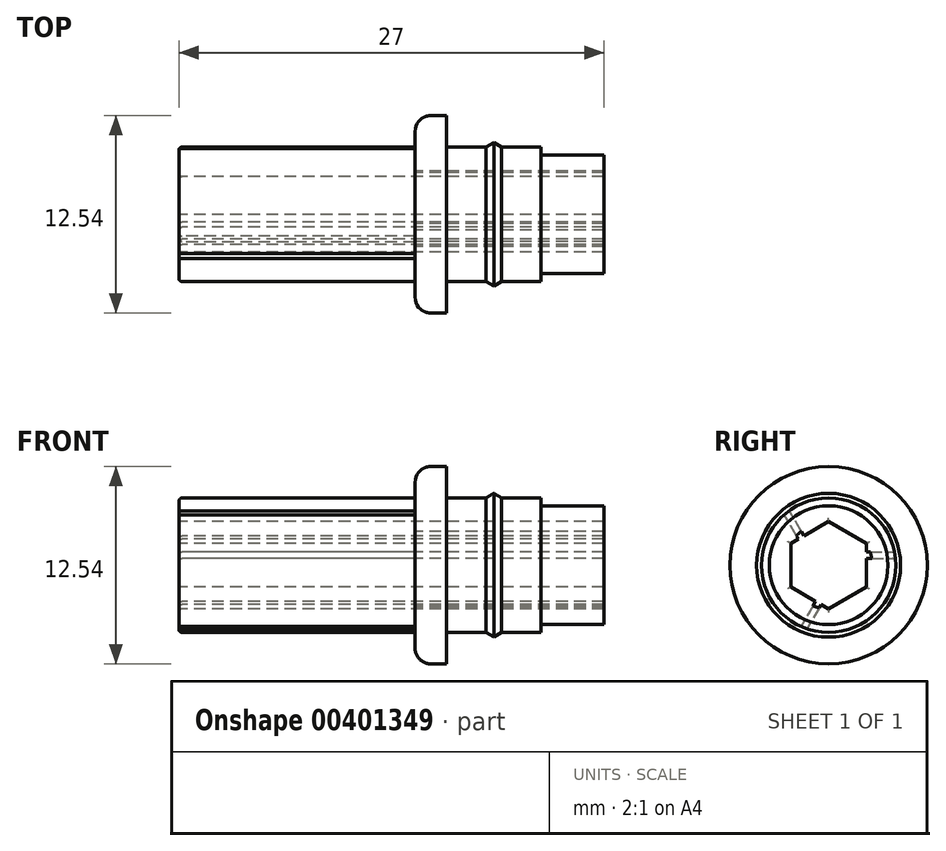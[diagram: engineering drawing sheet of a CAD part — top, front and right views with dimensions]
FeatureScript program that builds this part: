
annotation { "Feature Type Name" : "Feature", "Feature Type Description" : "" }
export const myFeature = defineFeature(function(context is Context, id is Id, definition is map)
    precondition{}
    {
        {
            var Q0;
            Q0=qCreatedBy(makeId("Front.planeOp"),FACE);
            var sketch = newSketch(context, id + "F0", { "sketchPlane" : qUnion([Q0])});
            skLineSegment(sketch, "E0", {"start": v(-9.05, 2.77) * mm, "end": v(17.95, 2.77) * mm});
            skLineSegment(sketch, "E1", {"start": v(7.95, 4.27) * mm, "end": v(7.95, 6.27) * mm});
            skLineSegment(sketch, "E2", {"start": v(7.95, 6.27) * mm, "end": v(5.95, 6.27) * mm});
            skLineSegment(sketch, "E3", {"start": v(5.95, 6.27) * mm, "end": v(5.95, 4.27) * mm});
            skLineSegment(sketch, "E4", {"start": v(5.95, 4.27) * mm, "end": v(-9.05, 4.27) * mm});
            skLineSegment(sketch, "E5", {"start": v(-9.05, 4.27) * mm, "end": v(-9.05, 2.77) * mm});
            skLineSegment(sketch, "E6", {"start": v(-9.05, 0) * mm, "end": v(13.38, 0) * mm});
            skLineSegment(sketch, "E7", {"start": v(10.45, 4.27) * mm, "end": v(7.95, 4.27) * mm});
            skLineSegment(sketch, "E8", {"start": v(10.45, 4.27) * mm, "end": v(10.95, 4.57) * mm});
            skLineSegment(sketch, "E9", {"start": v(10.95, 4.57) * mm, "end": v(11.45, 4.27) * mm});
            skLineSegment(sketch, "E10", {"start": v(11.45, 4.27) * mm, "end": v(13.95, 4.27) * mm});
            skLineSegment(sketch, "E11", {"start": v(13.95, 4.27) * mm, "end": v(13.95, 3.77) * mm});
            skLineSegment(sketch, "E12", {"start": v(13.95, 3.77) * mm, "end": v(17.95, 3.77) * mm});
            skLineSegment(sketch, "E13", {"start": v(17.95, 3.77) * mm, "end": v(17.95, 2.77) * mm});
            skSolve(sketch);
        }
        {
            var Q0;
            Q0=makeQuery(id+"F0.imprint","IMPRINT",FACE,{"disambiguationData":[TD([[makeQuery(id+"F0.imprint","IMPRINT",EDGE,{"derivedFrom":sQuery(id+"F0.wireOp",EDGE,"E0")}),1.0]])]});
            var Q1;
            Q1=sQuery(id+"F0.wireOp",EDGE,"E6");
            revolve(context, id + "F1", {"entities" : qUnion([Q0]), "axis" : qUnion([Q1]), "revolveType" : RevolveType.FULL});
        }
        {
            var Q0;
            Q0=makeQuery(id+"F1.opRevolve","SWEPT_EDGE",EDGE,{"disambiguationData":[OSD([sQuery(id+"F0.wireOp",EDGE,"E2"),sQuery(id+"F0.wireOp",EDGE,"E3")])]});
            fillet(context, id + "F2", {"entities" : qUnion([Q0]), "radius" : 1 * mm, "tangentPropagation" : true, "allowEdgeOverflow" : false});
        }
        {
            var Q0;
            Q0=makeQuery(id+"F1.opRevolve","SWEPT_FACE",FACE,{"disambiguationData":[OSD([sQuery(id+"F0.wireOp",EDGE,"E5")])]});
            var sketch = newSketch(context, id + "F3", { "sketchPlane" : qUnion([Q0])});
            skCircle(sketch, "E14.cCircle", {"center": v(0, 0) * mm, "radius": 2.4 * mm, "construction": true});
            skLineSegment(sketch, "E14.0", {"start": v(2.4, 1.38) * mm, "end": v(2.4, -1.38) * mm});
            skLineSegment(sketch, "E14.1", {"start": v(2.4, -1.38) * mm, "end": v(0, -2.77) * mm});
            skLineSegment(sketch, "E14.2", {"start": v(0, -2.77) * mm, "end": v(-2.4, -1.38) * mm});
            skLineSegment(sketch, "E14.3", {"start": v(-2.4, -1.38) * mm, "end": v(-2.4, 1.38) * mm});
            skLineSegment(sketch, "E14.4", {"start": v(-2.4, 1.38) * mm, "end": v(0, 2.77) * mm});
            skLineSegment(sketch, "E14.5", {"start": v(0, 2.77) * mm, "end": v(2.4, 1.38) * mm});
            skPoint(sketch, "E14.0.midPoint", {"position": v(2.4, 0) * mm});
            skLineSegment(sketch, "E15", {"start": v(1.58, 1.86) * mm, "end": v(2.5, 3.46) * mm});
            skLineSegment(sketch, "E16", {"start": v(1.92, 1.66) * mm, "end": v(2.82, 3.2) * mm});
            skLineSegment(sketch, "E17", {"start": v(0.82, -2.3) * mm, "end": v(1.75, -3.9) * mm});
            skLineSegment(sketch, "E18", {"start": v(0.48, -2.5) * mm, "end": v(1.37, -4.04) * mm});
            skLineSegment(sketch, "E19", {"start": v(-2.4, 0.83) * mm, "end": v(-4.19, 0.83) * mm});
            skLineSegment(sketch, "E20", {"start": v(-2.4, 0.43) * mm, "end": v(-4.25, 0.43) * mm});
            skSolve(sketch);
        }
        {
            var Q0;
            {var subQ0=sQuery(id+"F3.wireOp",EDGE,"E14.0");Q0=makeQuery(id+"F3.imprint","IMPRINT",FACE,{"disambiguationData":[TD([[makeQuery(id+"F3.imprint","IMPRINT",EDGE,{"derivedFrom":subQ0}),1.0]])]});}
            extrude(context, id + "F4", {"entities" : qUnion([Q0]), "operationType" : NewBodyOperationType.ADD, "depth" : -27 * mm});
        }
        {
            var Q0;
            {var subQ0=sQuery(id+"F3.wireOp",EDGE,"E14.1");Q0=makeQuery(id+"F3.imprint","IMPRINT",FACE,{"disambiguationData":[TD([[makeQuery(id+"F3.imprint","IMPRINT",EDGE,{"derivedFrom":subQ0}),1.0]])]});}
            var Q1;
            {var subQ0=sQuery(id+"F3.wireOp",EDGE,"E14.2");Q1=makeQuery(id+"F3.imprint","IMPRINT",FACE,{"disambiguationData":[TD([[makeQuery(id+"F3.imprint","IMPRINT",EDGE,{"derivedFrom":subQ0}),1.0]])]});}
            var Q2;
            {var subQ0=sQuery(id+"F3.wireOp",EDGE,"E14.3");Q2=makeQuery(id+"F3.imprint","IMPRINT",FACE,{"disambiguationData":[TD([[makeQuery(id+"F3.imprint","IMPRINT",EDGE,{"derivedFrom":subQ0}),1.0]])]});}
            var Q3;
            {var subQ0=sQuery(id+"F3.wireOp",EDGE,"E14.4");Q3=makeQuery(id+"F3.imprint","IMPRINT",FACE,{"disambiguationData":[TD([[makeQuery(id+"F3.imprint","IMPRINT",EDGE,{"derivedFrom":subQ0}),1.0]])]});}
            var Q4;
            {var subQ0=sQuery(id+"F3.wireOp",EDGE,"E14.5");Q4=makeQuery(id+"F3.imprint","IMPRINT",FACE,{"disambiguationData":[TD([[makeQuery(id+"F3.imprint","IMPRINT",EDGE,{"derivedFrom":subQ0}),1.0]])]});}
            var Q5;
            {var subQ0=sQuery(id+"F3.wireOp",EDGE,"E14.0");Q5=makeQuery(id+"F3.imprint","IMPRINT",FACE,{"disambiguationData":[TD([[makeQuery(id+"F3.imprint","IMPRINT",EDGE,{"derivedFrom":subQ0}),1.0]])]});}
            extrude(context, id + "F5", {"entities" : qUnion([Q0, Q1, Q2, Q3, Q4, Q5]), "operationType" : NewBodyOperationType.ADD, "depth" : -27 * mm});
        }
        {
            var Q0;
            {var subQ0=sQuery(id+"F3.wireOp",EDGE,"E15");var subQ1=sQuery(id+"F0.wireOp",EDGE,"E5");var subQ2=makeQuery(id+"F1.opRevolve","SWEPT_EDGE",EDGE,{"disambiguationData":[OSD([sQuery(id+"F0.wireOp",EDGE,"E4"),subQ1])]});var subQ3=makeQuery(id+"F3.imprint","INTERSECT",VERTEX,{"derivedFrom":[subQ2,subQ0]});Q0=makeQuery(id+"F3.imprint","IMPRINT",FACE,{"disambiguationData":[TD([[makeQuery(id+"F3.imprint","IMPRINT",EDGE,{"disambiguationData":[TD([[subQ3,1.0]])],"derivedFrom":subQ0}),-1.0]])]});}
            extrude(context, id + "F6", {"entities" : qUnion([Q0]), "operationType" : NewBodyOperationType.REMOVE, "oppositeDirection" : true, "depth" : 15 * mm});
        }
        {
            var Q0;
            {var subQ0=sQuery(id+"F3.wireOp",EDGE,"E17");var subQ1=sQuery(id+"F0.wireOp",EDGE,"E5");var subQ2=makeQuery(id+"F1.opRevolve","SWEPT_EDGE",EDGE,{"disambiguationData":[OSD([sQuery(id+"F0.wireOp",EDGE,"E4"),subQ1])]});var subQ3=makeQuery(id+"F3.imprint","INTERSECT",VERTEX,{"derivedFrom":[subQ2,subQ0]});Q0=makeQuery(id+"F3.imprint","IMPRINT",FACE,{"disambiguationData":[TD([[makeQuery(id+"F3.imprint","IMPRINT",EDGE,{"disambiguationData":[TD([[subQ3,1.0]])],"derivedFrom":subQ0}),-1.0]])]});}
            extrude(context, id + "F7", {"entities" : qUnion([Q0]), "operationType" : NewBodyOperationType.REMOVE, "oppositeDirection" : true, "depth" : 15 * mm});
        }
        {
            var Q0;
            {var subQ0=sQuery(id+"F3.wireOp",EDGE,"E19");var subQ1=sQuery(id+"F0.wireOp",EDGE,"E5");var subQ2=makeQuery(id+"F1.opRevolve","SWEPT_EDGE",EDGE,{"disambiguationData":[OSD([sQuery(id+"F0.wireOp",EDGE,"E4"),subQ1])]});var subQ3=makeQuery(id+"F3.imprint","INTERSECT",VERTEX,{"derivedFrom":[subQ2,subQ0]});Q0=makeQuery(id+"F3.imprint","IMPRINT",FACE,{"disambiguationData":[TD([[makeQuery(id+"F3.imprint","IMPRINT",EDGE,{"disambiguationData":[TD([[subQ3,1.0]])],"derivedFrom":subQ0}),1.0]])]});}
            extrude(context, id + "F8", {"entities" : qUnion([Q0]), "operationType" : NewBodyOperationType.REMOVE, "oppositeDirection" : true, "depth" : 15 * mm});
        }
        {
            var Q0;
            {var subQ0=sQuery(id+"F3.wireOp",EDGE,"E15");var subQ2=sQuery(id+"F0.wireOp",EDGE,"E5");var subQ6=sQuery(id+"F0.wireOp",EDGE,"E4");var subQ19=makeQuery(id+"F5.opExtrude","SWEPT_FACE",FACE,{"disambiguationData":[OSD([subQ0])]});Q0=makeQuery(id+"F8.boolean.opBoolean","SPLIT",EDGE,{"disambiguationData":[TD([subQ19])],"derivedFrom":makeQuery(id+"F7.boolean.opBoolean","SPLIT",EDGE,{"disambiguationData":[TD([subQ19])],"derivedFrom":makeQuery(id+"F1.opRevolve","SWEPT_EDGE",EDGE,{"disambiguationData":[OSD([subQ6,subQ2])]})})});}
            var Q1;
            {var subQ1=sQuery(id+"F0.wireOp",EDGE,"E5");var subQ3=sQuery(id+"F0.wireOp",EDGE,"E4");var subQ7=sQuery(id+"F3.wireOp",EDGE,"E16");Q1=makeQuery(id+"F7.boolean.opBoolean","SPLIT",EDGE,{"disambiguationData":[TD([makeQuery(id+"F5.opExtrude","SWEPT_FACE",FACE,{"disambiguationData":[OSD([subQ7])]})])],"derivedFrom":makeQuery(id+"F1.opRevolve","SWEPT_EDGE",EDGE,{"disambiguationData":[OSD([subQ3,subQ1])]})});}
            var Q2;
            {var subQ0=sQuery(id+"F3.wireOp",EDGE,"E15");var subQ2=sQuery(id+"F0.wireOp",EDGE,"E5");var subQ6=sQuery(id+"F0.wireOp",EDGE,"E4");var subQ10=sQuery(id+"F3.wireOp",EDGE,"E18");var subQ15=makeQuery(id+"F5.opExtrude","SWEPT_FACE",FACE,{"disambiguationData":[OSD([subQ10])]});Q2=makeQuery(id+"F8.boolean.opBoolean","SPLIT",EDGE,{"disambiguationData":[TD([subQ15])],"derivedFrom":makeQuery(id+"F7.boolean.opBoolean","SPLIT",EDGE,{"disambiguationData":[TD([makeQuery(id+"F5.opExtrude","SWEPT_FACE",FACE,{"disambiguationData":[OSD([subQ0])]})])],"derivedFrom":makeQuery(id+"F1.opRevolve","SWEPT_EDGE",EDGE,{"disambiguationData":[OSD([subQ6,subQ2])]})})});}
            var Q3;
            {var subQ0=sQuery(id+"F3.wireOp",EDGE,"E14.3");Q3=makeQuery(id+"F5.opExtrude","CAP_EDGE",EDGE,{"disambiguationData":[OSD([subQ0]),TDD([makeQuery(id+"F3.imprint","IMPRINT",EDGE,{"disambiguationData":[TD([[makeQuery(id+"F3.imprint","INTERSECT",VERTEX,{"derivedFrom":[subQ0,sQuery(id+"F3.wireOp",EDGE,"E20")]}),1.0]])],"derivedFrom":subQ0})])],"isStart":true});}
            var Q4;
            Q4=makeQuery(id+"F5.opExtrude","CAP_EDGE",EDGE,{"disambiguationData":[OSD([sQuery(id+"F3.wireOp",EDGE,"E14.2")])],"isStart":true});
            var Q5;
            {var subQ0=sQuery(id+"F3.wireOp",EDGE,"E14.1");Q5=makeQuery(id+"F5.opExtrude","CAP_EDGE",EDGE,{"disambiguationData":[OSD([subQ0]),TDD([makeQuery(id+"F3.imprint","IMPRINT",EDGE,{"disambiguationData":[TD([[makeQuery(id+"F3.imprint","INTERSECT",VERTEX,{"derivedFrom":[subQ0,sQuery(id+"F3.wireOp",EDGE,"E18")]}),-1.0]])],"derivedFrom":subQ0})])],"isStart":true});}
            var Q6;
            Q6=makeQuery(id+"F4.opExtrude","CAP_EDGE",EDGE,{"disambiguationData":[OSD([sQuery(id+"F3.wireOp",EDGE,"E14.0")])],"isStart":true});
            var Q7;
            {var subQ0=sQuery(id+"F3.wireOp",EDGE,"E14.5");Q7=makeQuery(id+"F5.opExtrude","CAP_EDGE",EDGE,{"disambiguationData":[OSD([subQ0]),TDD([makeQuery(id+"F3.imprint","IMPRINT",EDGE,{"disambiguationData":[TD([[makeQuery(id+"F3.imprint","INTERSECT",VERTEX,{"derivedFrom":[subQ0,sQuery(id+"F3.wireOp",EDGE,"E16")]}),-1.0]])],"derivedFrom":subQ0})])],"isStart":true});}
            var Q8;
            Q8=makeQuery(id+"F5.opExtrude","CAP_EDGE",EDGE,{"disambiguationData":[OSD([sQuery(id+"F3.wireOp",EDGE,"E14.4")])],"isStart":true});
            var Q9;
            {var subQ0=sQuery(id+"F3.wireOp",EDGE,"E14.5");Q9=makeQuery(id+"F5.opExtrude","CAP_EDGE",EDGE,{"disambiguationData":[OSD([subQ0]),TDD([makeQuery(id+"F3.imprint","IMPRINT",EDGE,{"disambiguationData":[TD([[makeQuery(id+"F3.imprint","INTERSECT",VERTEX,{"derivedFrom":[subQ0,sQuery(id+"F3.wireOp",EDGE,"E15")]}),1.0]])],"derivedFrom":subQ0})])],"isStart":true});}
            var Q10;
            {var subQ0=sQuery(id+"F3.wireOp",EDGE,"E14.1");Q10=makeQuery(id+"F5.opExtrude","CAP_EDGE",EDGE,{"disambiguationData":[OSD([subQ0]),TDD([makeQuery(id+"F3.imprint","IMPRINT",EDGE,{"disambiguationData":[TD([[makeQuery(id+"F3.imprint","INTERSECT",VERTEX,{"derivedFrom":[subQ0,sQuery(id+"F3.wireOp",EDGE,"E17")]}),1.0]])],"derivedFrom":subQ0})])],"isStart":true});}
            var Q11;
            {var subQ0=sQuery(id+"F3.wireOp",EDGE,"E14.3");Q11=makeQuery(id+"F5.opExtrude","CAP_EDGE",EDGE,{"disambiguationData":[OSD([subQ0]),TDD([makeQuery(id+"F3.imprint","IMPRINT",EDGE,{"disambiguationData":[TD([[makeQuery(id+"F3.imprint","INTERSECT",VERTEX,{"derivedFrom":[subQ0,sQuery(id+"F3.wireOp",EDGE,"E19")]}),-1.0]])],"derivedFrom":subQ0})])],"isStart":true});}
            fillet(context, id + "F9", {"entities" : qUnion([Q0, Q1, Q2, Q3, Q4, Q5, Q6, Q7, Q8, Q9, Q10, Q11]), "radius" : .2 * mm, "tangentPropagation" : true, "allowEdgeOverflow" : false});
        }
    });
